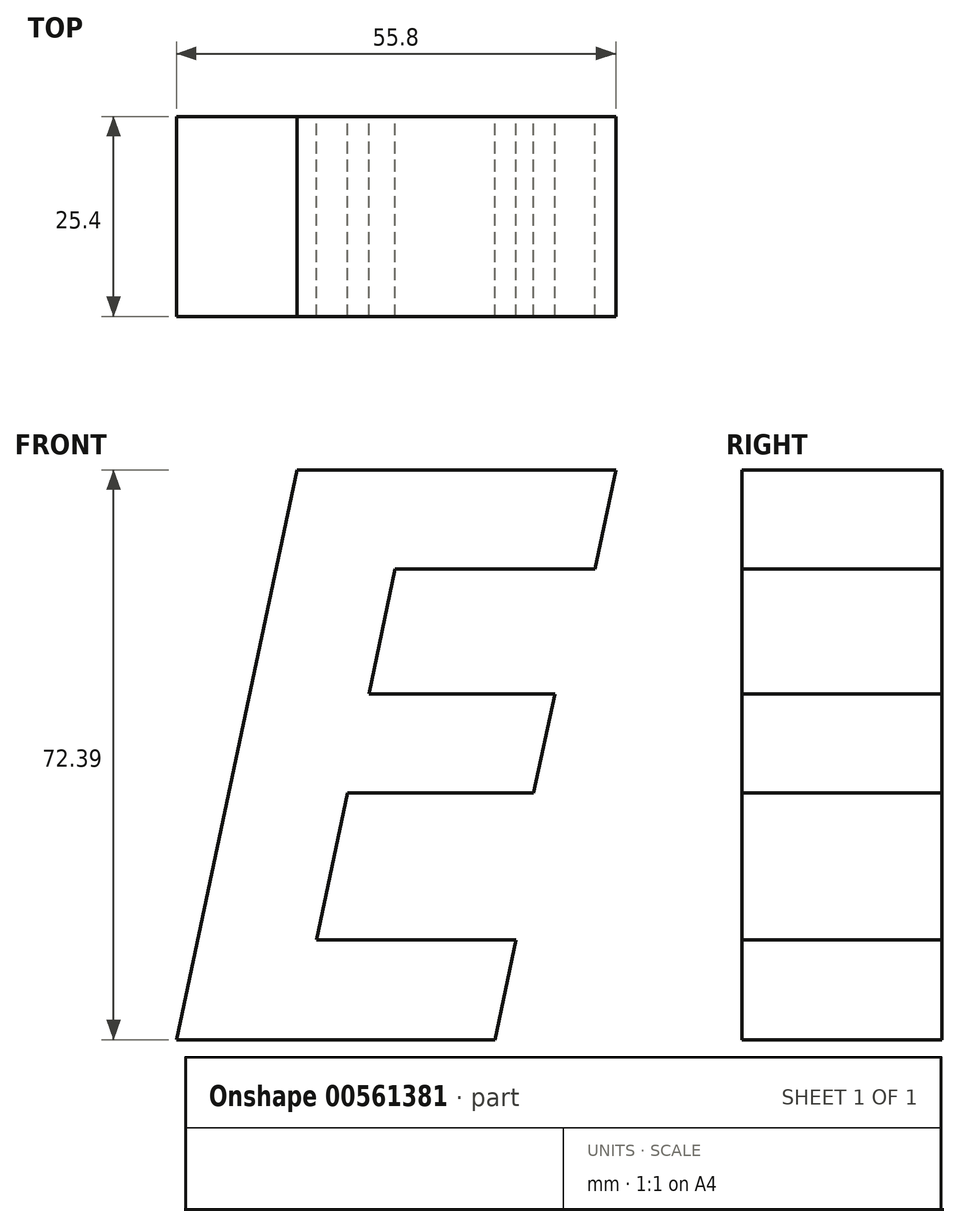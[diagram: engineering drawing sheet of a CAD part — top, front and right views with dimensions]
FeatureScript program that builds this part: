
annotation { "Feature Type Name" : "Feature", "Feature Type Description" : "" }
export const myFeature = defineFeature(function(context is Context, id is Id, definition is map)
    precondition{}
    {
        {
            var Q0;
            Q0=qCreatedBy(makeId("Front.planeOp"),FACE);
            var sketch = newSketch(context, id + "F0", { "sketchPlane" : qUnion([Q0])});
            skText(sketch, "E0", { "text": "E", "fontName": "OpenSans-BoldItalic.ttf"});
            const initialGuessF0  = {"E0": [-0.04863, -0.0501, 1, 0, 0.07301]};
            skSetInitialGuess(sketch, initialGuessF0);
            skSolve(sketch);
        }
        {
            var Q0;
            Q0=makeQuery(id+"F0.imprint","IMPRINT",FACE,{"disambiguationData":[TD([[makeQuery(id+"F0.imprint","IMPRINT",EDGE,{"derivedFrom":sQuery(id+"F0.wireOp",EDGE,"E0.sketch_text.stroke-0")}),-1.0]])]});
            extrude(context, id + "F1", {"entities" : qUnion([Q0]), "depth" : 25.4 * mm, "offsetDistance" : 25.4 * mm});
        }
    });
